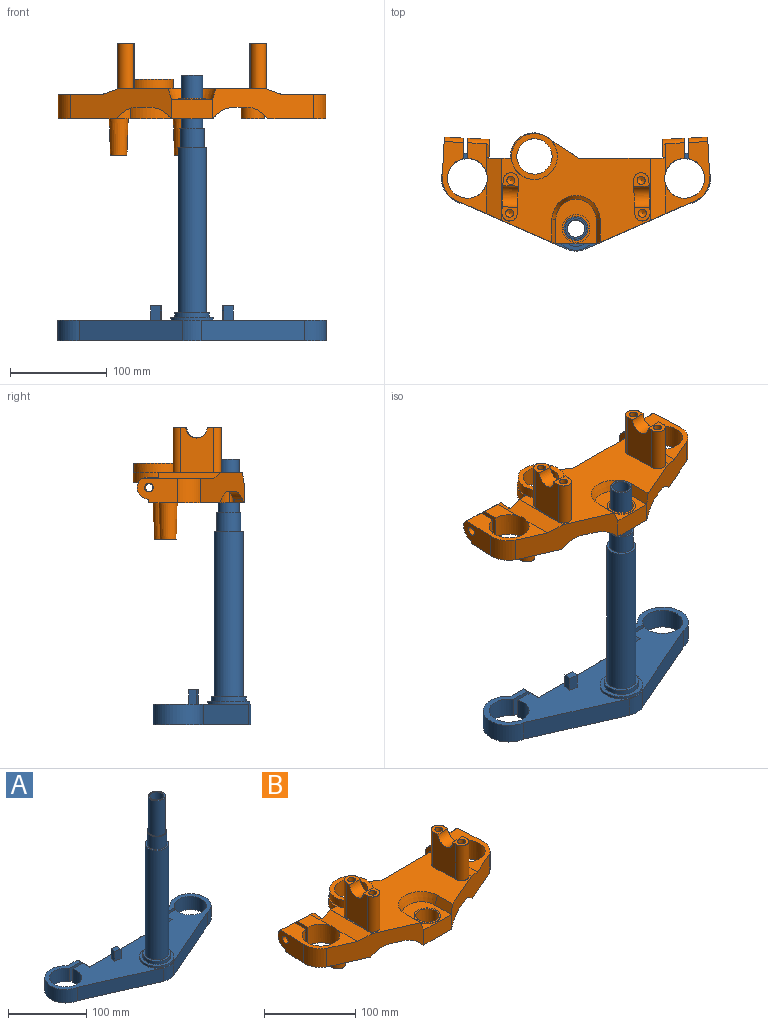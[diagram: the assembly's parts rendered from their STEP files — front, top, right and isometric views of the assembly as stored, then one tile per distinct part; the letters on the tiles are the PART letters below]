
ASSEMBLY  parts=2 mates=1
PART A: 66 faces, bbox 280x102.8x276.4 mm
  f0: cylinder r=3.32mm len=25mm, axis (0,-1,0), area 481.4mm2, adj f1,f2,f3,f5,f63
  f1: plane 158.51x13mm, normal (0,-1,0), area 2041.2mm2, adj f0,f2,f5,f6,f7,f58
  f2: cylinder r=36.08mm len=13mm, axis (0,0,1), area 118.8mm2, adj f0,f1,f3,f5,f8,f58
  f3: cone r=1.73mm half-angle=60deg, axis (0,1,0), area 7.1mm2, adj f0,f2,f5
  f4: cylinder r=11.95mm len=21mm, axis (0,1,0), area 307.7mm2, adj f19,f58,f59,f63
  f5: plane 174.13x43.54mm, normal (0,0,-1), area 4723.6mm2, adj f0,f1,f2,f3,f6,f7,f8,f29
  f6: cylinder r=36.08mm len=13mm, axis (0,0,1), area 118.7mm2, adj f1,f5,f7,f29,f36,f58
  f7: cylinder r=3.32mm len=25mm, axis (0,-1,0), area 481.4mm2, adj f1,f5,f6,f36,f60
  f8: cylinder r=5mm len=13mm, axis (0,0,1), area 119.8mm2, adj f2,f5,f34,f58
  f9: cylinder r=11.95mm len=21mm, axis (0,1,0), area 153.8mm2, adj f10,f58,f59,f62
  f10: plane 24.29x21mm, normal (0,1,0), area 408.7mm2, adj f9,f11,f37,f58,f59
  f11: cylinder r=26.4mm len=52.48mm, axis (0,0,1), area 2138mm2, adj f10,f12,f58,f59
  f12: plane 107.57x46.94mm, normal (-0.4,-0.92,0), area 2464.6mm2, adj f11,f13,f58,f59
  f13: cylinder r=23mm len=21mm, axis (0,0,1), area 409mm2, adj f12,f14,f58,f59
  f14: plane 107.57x46.94mm, normal (0.4,-0.92,0), area 2464.6mm2, adj f13,f15,f58,f59
  f15: cylinder r=26.4mm len=52.48mm, axis (0,0,1), area 2138mm2, adj f14,f16,f58,f59
  f16: plane 24.29x21mm, normal (0,1,0), area 408.7mm2, adj f15,f17,f38,f58,f59
  f17: cylinder r=11.95mm len=21mm, axis (0,1,0), area 153.8mm2, adj f16,f58,f59,f61
  f18: cylinder r=11.95mm len=21mm, axis (0,1,0), area 307.7mm2, adj f19,f58,f59,f60
  f19: plane 149.32x21mm, normal (0,1,0), area 2595.6mm2, adj f4,f18,f39,f40,f58,f59
  f20: cylinder r=22mm len=44mm, axis (0,0,1), area 414.7mm2, adj f41,f59
  f21: plane 15x7.87mm, normal (0.98,0.18,0), area 120mm2, adj f22,f24,f42,f59
  f22: plane 15x9.84mm, normal (0.18,-0.98,0), area 150mm2, adj f21,f23,f42,f59
  f23: plane 15x7.87mm, normal (-0.98,-0.18,0), area 120mm2, adj f22,f24,f42,f59
  f24: plane 15x9.84mm, normal (-0.18,0.98,0), area 150mm2, adj f21,f23,f42,f59
  f25: plane 15x9.84mm, normal (-0.18,-0.98,0), area 150mm2, adj f26,f28,f43,f59
  f26: plane 15x7.87mm, normal (-0.98,0.18,0), area 120mm2, adj f25,f27,f43,f59
  f27: plane 15x9.84mm, normal (0.18,0.98,0), area 150mm2, adj f26,f28,f43,f59
  f28: plane 15x7.87mm, normal (0.98,-0.18,0), area 120mm2, adj f25,f27,f43,f59
  f29: cylinder r=5mm len=13mm, axis (0,0,1), area 119.8mm2, adj f5,f6,f30,f58
  f30: plane 52.81x23.8mm, normal (-0.41,0.91,0), area 753mm2, adj f5,f29,f31,f58
  f31: cylinder r=5.48mm len=13mm, axis (0,0,1), area 136.2mm2, adj f5,f30,f32,f58
  f32: cylinder r=23mm len=45.84mm, axis (0,0,1), area 889.9mm2, adj f5,f31,f33,f58
  f33: cylinder r=5.48mm len=13mm, axis (0,0,1), area 136.2mm2, adj f5,f32,f34,f58
  f34: plane 52.81x23.8mm, normal (0.41,0.91,0), area 753mm2, adj f5,f8,f33,f58
  f35: cylinder r=9mm len=275mm, axis (0,0,1), area 15550.9mm2, adj f44,f58
  f36: cone r=1.73mm half-angle=60deg, axis (0,1,0), area 8.9mm2, adj f5,f6,f7
  f37: cylinder r=4.5mm len=9mm, axis (0,1,0), area 169.6mm2, adj f10,f62
  f38: cylinder r=4.5mm len=9mm, axis (0,1,0), area 169.6mm2, adj f16,f61
  f39: cone r=7.5mm half-angle=10deg, axis (0,-1,0), area 225.2mm2, adj f19,f45
  f40: cone r=7.5mm half-angle=10deg, axis (0,-1,0), area 225.2mm2, adj f19,f46
  f41: plane 44x44mm, normal (0,0,1), area 502.7mm2, adj f20,f47
  f42: plane 11.27x9.66mm, normal (0,0,1), area 80mm2, adj f21,f22,f23,f24
  f43: plane 11.27x9.66mm, normal (0,0,1), area 80mm2, adj f25,f26,f27,f28
  f44: plane 22x22mm, normal (0,0,1), area 125.7mm2, adj f35,f48
  f45: plane 13.24x13.24mm, normal (0,1,0), area 118.6mm2, adj f39,f49
  f46: plane 13.24x13.24mm, normal (0,1,0), area 118.6mm2, adj f40,f50
  f47: cylinder r=18mm len=36mm, axis (0,0,1), area 565.5mm2, adj f41,f51
  f48: cylinder r=11mm len=55mm, axis (0,0,1), area 3801.3mm2, adj f44,f52
  f49: cylinder r=2.46mm len=10mm, axis (0,-1,0), area 154.5mm2, adj f45,f53
  f50: cylinder r=2.46mm len=10mm, axis (0,-1,0), area 154.5mm2, adj f46,f54
  f51: plane 36x36mm, normal (0,0,1), area 311mm2, adj f47,f55
  f52: plane 25x25mm, normal (0,0,1), area 110.7mm2, adj f48,f56
  f53: cone r=1.73mm half-angle=60deg, axis (0,1,0), area 21.9mm2, adj f49
  f54: cone r=1.73mm half-angle=60deg, axis (0,1,0), area 21.9mm2, adj f50
  f55: cylinder r=15mm len=171mm, axis (0,0,1), area 16116.4mm2, adj f51,f57
  f56: cylinder r=12.5mm len=25mm, axis (0,0,1), area 1570.8mm2, adj f52,f57
  f57: plane 30x30mm, normal (0,0,1), area 216mm2, adj f55,f56
  f58: plane 278.61x101.45mm, normal (0,0,-1), area 7007.3mm2, adj f1,f2,f4,f6,f8,f9,f10,f11
  f59: plane 278.61x101.45mm, normal (0,0,1), area 10329.1mm2, adj f4,f9,f10,f11,f12,f13,f14,f15
  f60: plane 24.67x21mm, normal (0,1,0), area 445.5mm2, adj f7,f18,f58,f59,f65
  f61: plane 26.61x21mm, normal (0,-1,0), area 457.4mm2, adj f17,f38,f58,f59,f65
  f62: plane 26.61x21mm, normal (0,-1,0), area 457.4mm2, adj f9,f37,f58,f59,f64
  f63: plane 24.67x21mm, normal (0,1,0), area 445.5mm2, adj f0,f4,f58,f59,f64
  f64: cylinder r=20.7mm len=41.4mm, axis (0,0,1), area 2637.7mm2, adj f58,f59,f62,f63
  f65: cylinder r=20.7mm len=41.4mm, axis (0,0,1), area 2637.7mm2, adj f58,f59,f60,f61
PART B: 133 faces, bbox 278x115.8x116.7 mm
  f0: plane 17x17mm, normal (0,0,-1), area 227mm2, adj f1
  f1: cylinder r=8.5mm len=17mm, axis (0,0,-1), area 854.5mm2, adj f0,f2
  f2: plane 24x24mm, normal (0,0,-1), area 225.4mm2, adj f1,f3
  f3: cylinder r=12mm len=24mm, axis (0,0,-1), area 904.8mm2, adj f2,f4
  f4: torus R=16mm, axis (0,0,-1), area 531.1mm2, adj f3,f5
  f5: plane 179.81x63.04mm, normal (0,0,-1), area 5661mm2, adj f4,f6,f7,f8,f9,f10,f11,f12
  f6: torus R=34.67mm, axis (0,0,-1), area 130.5mm2, adj f5,f7,f17,f18
  f7: torus R=21.83mm, axis (0,0,-1), area 112.8mm2, adj f5,f6,f8,f19
  f8: torus R=36.47mm, axis (0,0,-1), area 312mm2, adj f5,f7,f9,f20
  f9: torus R=21.83mm, axis (0,0,-1), area 208.8mm2, adj f5,f8,f10,f21
  f10: cylinder r=4mm len=79.46mm, axis (-1,0,0), area 471.9mm2, adj f5,f9,f11,f22
  f11: bspline ~14.54x7.04mm, area 68.5mm2, adj f5,f10,f12,f23
  f12: revolved ~28.67x18.9mm, area 180.2mm2, adj f5,f11,f13,f24
  f13: cylinder r=4mm len=76.66mm, axis (0.92,0.4,0), area 492.4mm2, adj f5,f12,f14,f25
  f14: revolved ~7.03x6.26mm, area 48.4mm2, adj f5,f13,f15,f26
  f15: torus R=21.1mm, axis (0,0,-1), area 375.7mm2, adj f5,f14,f16,f27
  f16: revolved ~7x5.19mm, area 45mm2, adj f5,f15,f17,f28
  f17: cylinder r=4mm len=73.98mm, axis (-0.92,0.4,0), area 475.3mm2, adj f5,f6,f16,f29
  f18: cylinder r=30.67mm len=20.11mm, axis (0,0,-1), area 300.1mm2, adj f6,f19,f29,f30
  f19: cylinder r=17.83mm len=18.64mm, axis (0,0,-1), area 239.1mm2, adj f7,f18,f20,f30
  f20: cylinder r=32.47mm len=45.31mm, axis (0,0,-1), area 605mm2, adj f8,f19,f21,f30
  f21: cylinder r=17.83mm len=26.55mm, axis (0,0,-1), area 402mm2, adj f9,f20,f22,f30
  f22: plane 79.46x12mm, normal (0,-1,0), area 447.3mm2, adj f10,f21,f23,f30,f31,f32,f33,f34
  f23: cylinder r=28.7mm len=12.7mm, axis (0,0,-1), area 157.9mm2, adj f11,f22,f24,f31
  f24: cylinder r=28.7mm len=25.17mm, axis (0,0,-1), area 368.2mm2, adj f12,f23,f25,f31
  f25: plane 75.87x33.57mm, normal (-0.4,0.92,0), area 433.3mm2, adj f13,f24,f26,f31,f37,f38,f39,f40
  f26: cylinder r=5mm len=12mm, axis (0,0,-1), area 124.5mm2, adj f14,f25,f27,f37,f42
  f27: cylinder r=17.1mm len=34.2mm, axis (0,0,-1), area 659.8mm2, adj f15,f26,f28,f42
  f28: cylinder r=5mm len=12mm, axis (0,0,-1), area 118.3mm2, adj f16,f27,f29,f42,f43
  f29: plane 73.2x32.41mm, normal (0.4,0.92,0), area 398.6mm2, adj f17,f18,f28,f30,f43,f44,f45,f46
  f30: plane 160.39x73.49mm, normal (0,0,-1), area 2612.4mm2, adj f18,f19,f20,f21,f22,f29,f36,f47
  f31: plane 73.49x59.89mm, normal (0,0,-1), area 1557.8mm2, adj f22,f23,f24,f25,f32,f41,f55,f62
  f32: plane 8x6.42mm, normal (-0.67,0,-0.74), area 69.4mm2, adj f22,f31,f33,f55
  f33: cylinder r=23.19mm len=15.6mm, axis (0,-1,0), area 136.9mm2, adj f22,f32,f34,f55
  f34: plane 12.37x8mm, normal (0,0,-1), area 99mm2, adj f22,f33,f35,f55
  f35: cylinder r=26.58mm len=19.67mm, axis (0,-1,0), area 177.2mm2, adj f22,f34,f36,f55
  f36: plane 8x3.16mm, normal (0.74,0,-0.67), area 34.2mm2, adj f22,f30,f35,f55
  f37: plane 10.04x3.22mm, normal (0.74,0,-0.67), area 38mm2, adj f25,f26,f38,f42,f65
  f38: cylinder r=26.58mm len=19.67mm, axis (0,-1,0), area 193.3mm2, adj f25,f37,f39,f65
  f39: plane 14.13x12.37mm, normal (0,0,-1), area 108mm2, adj f25,f38,f40,f65
  f40: cylinder r=23.19mm len=15.6mm, axis (0,-1,0), area 149.3mm2, adj f25,f39,f41,f65
  f41: plane 11.53x6.42mm, normal (-0.67,0,-0.74), area 75.7mm2, adj f25,f31,f40,f65
  f42: plane 43.57x33.03mm, normal (0,0,-1), area 615.6mm2, adj f26,f27,f28,f37,f43,f56,f65,f68
  f43: plane 10.46x3.22mm, normal (-0.74,0,-0.67), area 39.8mm2, adj f28,f29,f42,f44,f56
  f44: cylinder r=26.59mm len=19.67mm, axis (0,1,0), area 202.6mm2, adj f29,f43,f45,f56
  f45: plane 14.55x12.37mm, normal (0,0,-1), area 113.2mm2, adj f29,f44,f46,f56
  f46: cylinder r=23.19mm len=15.96mm, axis (0,1,0), area 156.6mm2, adj f29,f45,f47,f56
  f47: plane 11.95x6.42mm, normal (0.67,0,-0.74), area 79.4mm2, adj f29,f30,f46,f56
  f48: cylinder r=20.7mm len=41.4mm, axis (0,0,-1), area 3141.1mm2, adj f30,f70,f71,f72,f129,f132
  f49: cylinder r=30.7mm len=21.99mm, axis (0,0,-1), area 120mm2, adj f30,f50,f73,f129
  f50: plane 30.9x22.2mm, normal (0,1,0), area 489.8mm2, adj f30,f49,f51,f71,f74,f75,f76,f77
  f51: cylinder r=10mm len=20.3mm, axis (0,0,1), area 247.6mm2, adj f30,f50,f52,f76
  f52: cylinder r=24.47mm len=47.12mm, axis (0,0,-1), area 1303.7mm2, adj f30,f51,f53,f76
  f53: cylinder r=10mm len=20.3mm, axis (0,0,-1), area 403mm2, adj f30,f52,f54,f76
  f54: plane 37.71x30.9mm, normal (0.55,0.84,0), area 644.6mm2, adj f30,f53,f55,f76,f77,f78,f80
  f55: plane 87.52x30.9mm, normal (0,1,0), area 2163.5mm2, adj f30,f31,f32,f33,f34,f35,f36,f54
  f56: plane 105.47x46.46mm, normal (-0.4,-0.92,0), area 2685mm2, adj f30,f42,f43,f44,f45,f46,f47,f57
  f57: cylinder r=25.7mm len=24.9mm, axis (0,0,-1), area 704.5mm2, adj f30,f56,f58,f70
  f58: plane 41.37x24.9mm, normal (-1,0.05,0), area 882.3mm2, adj f30,f57,f59,f70,f86,f87
  f59: plane 20.84x3.5mm, normal (0,1,0), area 72.2mm2, adj f30,f58,f86,f132
  f60: cone r=8.5mm half-angle=2deg, axis (0,0,1), area 2189.2mm2, adj f30,f88
  f61: cone r=8.5mm half-angle=2deg, axis (0,0,1), area 2189.2mm2, adj f30,f89
  f62: plane 20.84x3.5mm, normal (0,1,0), area 72.2mm2, adj f31,f63,f90,f131
  f63: plane 41.37x24.9mm, normal (1,0.05,0), area 882.3mm2, adj f31,f62,f64,f90,f91,f92
  f64: cylinder r=25.7mm len=24.9mm, axis (0,0,-1), area 704.5mm2, adj f31,f63,f65,f91
  f65: plane 105.47x46.46mm, normal (0.4,-0.92,0), area 2685.1mm2, adj f31,f37,f38,f39,f40,f41,f42,f64
  f66: cylinder r=30.7mm len=21.99mm, axis (0,0,-1), area 120mm2, adj f31,f55,f94,f130
  f67: cylinder r=20.7mm len=41.4mm, axis (0,0,-1), area 3141.1mm2, adj f31,f83,f91,f95,f130,f131
  f68: plane 42x19.9mm, normal (0,-1,0), area 835.8mm2, adj f42,f56,f65,f96
  f69: cylinder r=12.5mm len=25mm, axis (0,0,-1), area 1641.5mm2, adj f42,f97
  f70: plane 74.67x45.67mm, normal (0,0,1), area 1045mm2, adj f48,f56,f57,f58,f71,f86,f132
  f71: plane 79.66x16.31mm, normal (-0.34,0,0.94), area 1078.1mm2, adj f48,f50,f56,f70,f72,f73,f74,f75
  f72: plane 30.27x19.29mm, normal (0,0,1), area 376.1mm2, adj f48,f71,f73,f129
  f73: cylinder r=12mm len=23.99mm, axis (1,-0.05,0), area 713.7mm2, adj f49,f71,f72,f75,f129
  f74: cylinder r=30.7mm len=1.14mm, axis (0,0,-1), area 0.9mm2, adj f50,f71,f98
  f75: plane 22.92x19.8mm, normal (1,-0.05,0), area 329.2mm2, adj f50,f71,f73,f98,f99
  f76: plane 71.86x48.95mm, normal (0,0,-1), area 927.5mm2, adj f50,f51,f52,f53,f54,f77,f100
  f77: cylinder r=24.47mm len=33.11mm, axis (0,0,-1), area 520.7mm2, adj f50,f54,f76,f78
  f78: plane 153.72x113.26mm, normal (0,0,1), area 7980.7mm2, adj f50,f54,f55,f56,f65,f77,f79,f84
  f79: plane 64.32x0.13mm, normal (-0.94,0,-0.34), area 9.1mm2, adj f50,f56,f71,f78
  f80: plane 6.13x4.02mm, normal (0,0,-1), area 1.4mm2, adj f54,f101
  f81: plane 22.92x19.8mm, normal (-1,-0.05,0), area 329.2mm2, adj f55,f83,f94,f111,f112
  f82: cylinder r=30.7mm len=1.14mm, axis (0,0,-1), area 0.9mm2, adj f55,f83,f111
  f83: plane 79.66x16.31mm, normal (0.34,0,0.94), area 1078.1mm2, adj f55,f65,f67,f81,f82,f84,f91,f94
  f84: plane 64.32x0.13mm, normal (0.94,0,-0.34), area 9.1mm2, adj f55,f65,f78,f83
  f85: plane 25.11x11mm, normal (0.94,0,0.34), area 283.7mm2, adj f56,f78,f96,f102
  f86: cylinder r=12mm len=21.45mm, axis (1,-0.05,0), area 597.9mm2, adj f58,f59,f70,f132
  f87: cylinder r=4.5mm len=21.54mm, axis (1,-0.05,0), area 590.1mm2, adj f58,f132
  f88: plane 17x17mm, normal (0,0,-1), area 227mm2, adj f60
  f89: plane 17x17mm, normal (0,0,-1), area 227mm2, adj f61
  f90: cylinder r=12mm len=21.45mm, axis (1,0.05,0), area 597.9mm2, adj f62,f63,f91,f131
  f91: plane 74.67x45.67mm, normal (0,0,1), area 1045mm2, adj f63,f64,f65,f67,f83,f90,f131
  f92: cylinder r=4.5mm len=21.54mm, axis (1,0.05,0), area 590.1mm2, adj f63,f131
  f93: plane 25.11x11mm, normal (-0.94,0,0.34), area 283.7mm2, adj f65,f78,f96,f102
  f94: cylinder r=12mm len=23.99mm, axis (1,0.05,0), area 713.8mm2, adj f66,f81,f83,f95,f130
  f95: plane 30.27x19.29mm, normal (0,0,1), area 376.1mm2, adj f67,f83,f94,f130
  f96: plane 46.11x42mm, normal (0,0,1), area 1087mm2, adj f68,f85,f93,f102,f113
  f97: plane 29x29mm, normal (0,0,1), area 169.6mm2, adj f69,f113
  f98: cylinder r=12mm len=1.77mm, axis (1,-0.05,0), area 1.1mm2, adj f71,f74,f75
  f99: cylinder r=4.19mm len=22.69mm, axis (1,0,0), area 592.1mm2, adj f75,f129
  f100: cylinder r=18.3mm len=36.6mm, axis (0,0,-1), area 2368.6mm2, adj f76,f114
  f101: cylinder r=23.8mm len=47.6mm, axis (0,0,-1), area 1495.4mm2, adj f78,f80,f114
  f102: cone r=0.36mm half-angle=20deg, axis (0,0,1), area 845.9mm2, adj f78,f85,f93,f96
  f103: cylinder r=8.03mm len=47mm, axis (0,0,-1), area 1106.8mm2, adj f78,f104,f106,f115
  f104: plane 47x33.98mm, normal (-1,0.04,0), area 1407.9mm2, adj f78,f103,f105,f115,f116,f117
  f105: cylinder r=8.03mm len=47mm, axis (0,0,-1), area 1265mm2, adj f78,f104,f106,f116
  f106: plane 47x33.98mm, normal (1,-0.04,0), area 1407.9mm2, adj f78,f103,f105,f115,f116,f117
  f107: plane 47x33.98mm, normal (1,0.04,0), area 1407.9mm2, adj f78,f108,f110,f118,f119,f120
  f108: cylinder r=8.03mm len=47mm, axis (0,0,-1), area 1106.8mm2, adj f78,f107,f109,f118
  f109: plane 47x33.98mm, normal (-1,-0.04,0), area 1407.9mm2, adj f78,f108,f110,f118,f119,f120
  f110: cylinder r=8.03mm len=47mm, axis (0,0,-1), area 1265mm2, adj f78,f107,f109,f119
  f111: cylinder r=12mm len=1.77mm, axis (1,0.05,0), area 1.1mm2, adj f81,f82,f83
  f112: cylinder r=4.19mm len=22.69mm, axis (-1,0,0), area 592.1mm2, adj f81,f130
  f113: cylinder r=14.5mm len=29mm, axis (0,0,-1), area 91.1mm2, adj f96,f97
  f114: plane 47.6x47.6mm, normal (0,0,1), area 727.4mm2, adj f100,f101
  f115: plane 16.15x13.95mm, normal (0,0,1), area 135.3mm2, adj f103,f104,f106,f117,f121
  f116: plane 16.12x14.71mm, normal (0,0,1), area 147.8mm2, adj f104,f105,f106,f117,f122
  f117: cylinder r=11mm len=22.59mm, axis (-1,0.04,0), area 549mm2, adj f104,f106,f115,f116
  f118: plane 16.17x14.32mm, normal (0,0,1), area 141.4mm2, adj f107,f108,f109,f120,f123
  f119: plane 16.11x14.33mm, normal (0,0,1), area 141.7mm2, adj f107,f109,f110,f120,f124
  f120: cylinder r=11mm len=22.59mm, axis (-1,-0.04,0), area 549mm2, adj f107,f109,f118,f119
  f121: cylinder r=4.19mm len=30mm, axis (0,0,-1), area 789.4mm2, adj f115,f125
  f122: cylinder r=4.19mm len=30mm, axis (0,0,-1), area 789.4mm2, adj f116,f126
  f123: cylinder r=4.19mm len=30mm, axis (0,0,-1), area 789.4mm2, adj f118,f127
  f124: cylinder r=4.19mm len=30mm, axis (0,0,-1), area 789.4mm2, adj f119,f128
  f125: cone r=1.73mm half-angle=60deg, axis (0,0,1), area 63.6mm2, adj f121
  f126: cone r=1.73mm half-angle=60deg, axis (0,0,1), area 63.6mm2, adj f122
  f127: cone r=1.73mm half-angle=60deg, axis (0,0,1), area 63.6mm2, adj f123
  f128: cone r=1.73mm half-angle=60deg, axis (0,0,1), area 63.6mm2, adj f124
  f129: plane 25.14x20.98mm, normal (-1,0,0), area 380.2mm2, adj f30,f48,f49,f72,f73,f99
  f130: plane 25.14x20.98mm, normal (1,0,0), area 380.2mm2, adj f31,f66,f67,f94,f95,f112
  f131: plane 25.14x21.51mm, normal (-1,0,0), area 384.1mm2, adj f31,f62,f67,f90,f91,f92
  f132: plane 25.14x21.51mm, normal (1,0,0), area 384.1mm2, adj f30,f48,f59,f70,f86,f87
PLACE A t=(-41.63,20.28,-110.72)mm
PLACE B t=(-41.63,20.28,-109.62)mm fixed
MATE fastened A.f13 <-> B.f27  axis (0,0,1) through (-41.63,20.28,153.78)mm
